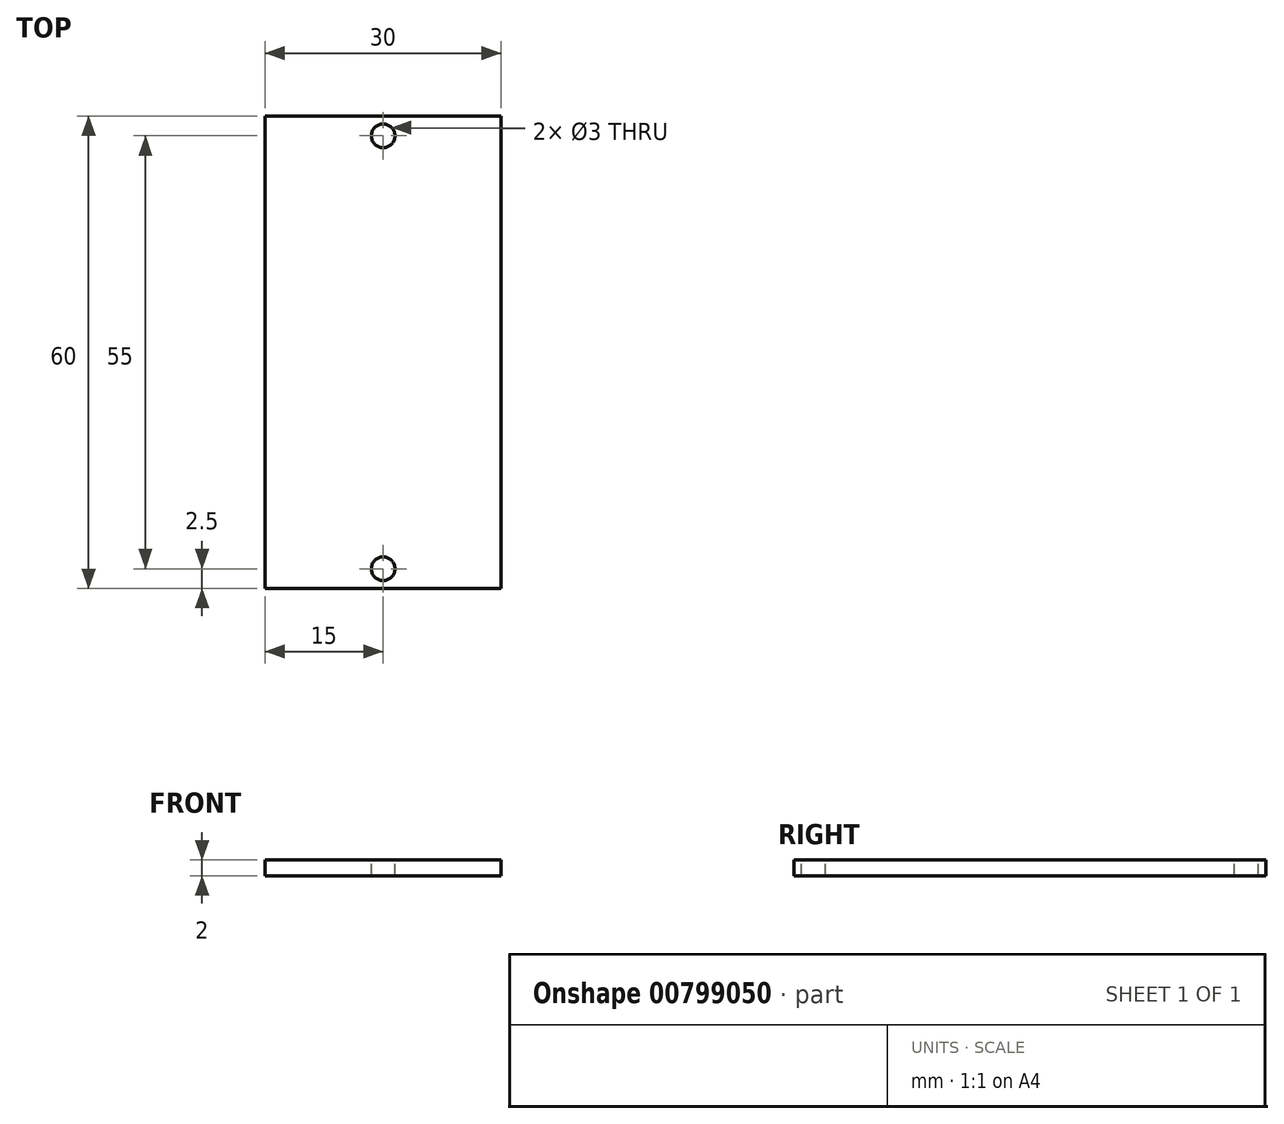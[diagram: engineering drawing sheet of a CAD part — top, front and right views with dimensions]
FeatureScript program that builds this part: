
annotation { "Feature Type Name" : "Feature", "Feature Type Description" : "" }
export const myFeature = defineFeature(function(context is Context, id is Id, definition is map)
    precondition{}
    {
        {
            var Q0;
            Q0=qCreatedBy(makeId("Top.planeOp"),FACE);
            var sketch = newSketch(context, id + "F0", { "sketchPlane" : qUnion([Q0])});
            skLineSegment(sketch, "E0.bottom", {"start": v(-15, 30) * mm, "end": v(15, 30) * mm});
            skLineSegment(sketch, "E0.top", {"start": v(-15, -30) * mm, "end": v(15, -30) * mm});
            skLineSegment(sketch, "E0.left", {"start": v(-15, 30) * mm, "end": v(-15, -30) * mm});
            skLineSegment(sketch, "E0.right", {"start": v(15, 30) * mm, "end": v(15, -30) * mm});
            skPoint(sketch, "E0.middle", {"position": v(0, 0) * mm});
            skSolve(sketch);
        }
        {
            var Q0;
            Q0=makeQuery(id+"F0.imprint","IMPRINT",FACE,{"disambiguationData":[TD([[makeQuery(id+"F0.imprint","IMPRINT",EDGE,{"derivedFrom":sQuery(id+"F0.wireOp",EDGE,"E0.bottom")}),-1.0]])]});
            extrude(context, id + "F1", {"entities" : qUnion([Q0]), "depth" : 2 * mm, "offsetDistance" : 25 * mm});
        }
        {
            var Q0;
            Q0=makeQuery(id+"F1.opExtrude","CAP_FACE",FACE,{"disambiguationData":[OSD([sQuery(id+"F0.wireOp",EDGE,"E0.bottom"),sQuery(id+"F0.wireOp",EDGE,"E0.top"),sQuery(id+"F0.wireOp",EDGE,"E0.left"),sQuery(id+"F0.wireOp",EDGE,"E0.right")])],"isStart":false});
            var sketch = newSketch(context, id + "F2", { "sketchPlane" : qUnion([Q0])});
            skLineSegment(sketch, "E1", {"start": v(0, 30) * mm, "end": v(0, 27.5) * mm});
            skCircle(sketch, "E2", {"center": v(0, 27.5) * mm, "radius": 1.5 * mm});
            skLineSegment(sketch, "E3", {"start": v(0, -30) * mm, "end": v(0, -27.5) * mm});
            skCircle(sketch, "E4", {"center": v(0, -27.5) * mm, "radius": 1.5 * mm});
            skSolve(sketch);
        }
        {
            var Q0;
            Q0=makeQuery(id+"F2.imprint","IMPRINT",FACE,{"disambiguationData":[TD([[makeQuery(id+"F2.imprint","IMPRINT",EDGE,{"derivedFrom":sQuery(id+"F2.wireOp",EDGE,"E4")}),1.0]])]});
            var Q1;
            Q1=makeQuery(id+"F2.imprint","IMPRINT",FACE,{"disambiguationData":[TD([[makeQuery(id+"F2.imprint","IMPRINT",EDGE,{"derivedFrom":sQuery(id+"F2.wireOp",EDGE,"E2")}),1.0]])]});
            extrude(context, id + "F3", {"entities" : qUnion([Q0, Q1]), "operationType" : NewBodyOperationType.REMOVE, "oppositeDirection" : true, "depth" : 25 * mm, "offsetDistance" : 25 * mm});
        }
    });
